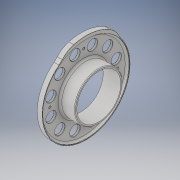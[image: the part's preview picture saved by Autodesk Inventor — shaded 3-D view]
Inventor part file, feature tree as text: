
AUTODESK INVENTOR PART (.ipt)
format: ipt  version: 2018 (Build 220112000, 112)  size: 302,592 bytes
history: native  units: mm
features: extrude x3, fillet x3, sketch x2, hole x2, chamfer x2, pattern_circular x2, other x1
ambient origin geometry x8: Origin, YZ Plane, XZ Plane, XY Plane, X Axis, Y Axis, Z Axis, Center Point
bodies: Solid1 (feature_tree)
feature tree (15):
  sketch  "Sketch1"  dims[d0=35.0mm d1=38.0mm]
  extrude  "Extrusion1"  Depth=38.0mm
  extrude  "Extrusion2"  Depth=0.1mm
  extrude  "Extrusion3"  Depth=0.1mm
  sketch  "Sketch2"  dims[d2=69.0mm d3=70.1mm d4=74.12mm d5=5.295329mm d6=6.675884mm d7=37.06mm d8=8.182104mm d9=5.506514mm d10=5.506514mm d11=1.507964mm d12=20.6mm d13=19.09mm d14=19.06mm d15=20.92mm d16=4.0mm d17=0.0mm d18=14.0mm d19=0.0mm d20=2.0mm d21=0.0mm d22=27.0mm d23=26.08mm d24=6.99mm d25=8.0mm d26=6.35mm d27=4.0mm d28=2.0mm d29=90.0deg d30=8.0mm d31=0.0mm d32=1.567mm d33=4.0mm d34=4.0mm d35=2.0mm d36=90.0deg d37=6.3mm d38=0.0mm d39=0.25mm d40=2.0mm d41=45.0deg d42=0.25mm d43=2.0mm d44=45.0deg d45=120.0mm d46=360.0deg d48=30.0mm d49=180.0deg d51=1.5mm d53=0.5mm d54=0.1mm]
  hole  "Hole1"  [1 undecoded]
  hole  "Hole2"  [1 undecoded]
  chamfer  "Chamfer1"  Distance=8.182104mm
  chamfer  "Chamfer2"  Distance=5.506514mm
  other  "Work Axis1"
  pattern_circular  "Circular Pattern1"  [2 undecoded]
  pattern_circular  "Circular Pattern2"  [2 undecoded]
  fillet  "Fillet1"  Radius=20.6mm
  fillet  "Fillet3"  Radius=19.09mm
  fillet  "Fillet4"  Radius=19.06mm
note: 6 required parameter values undecoded (feature->parameter linkage not recoverable at this tier; creation-order binding heuristic only, values carry confidence <= 0.55)
